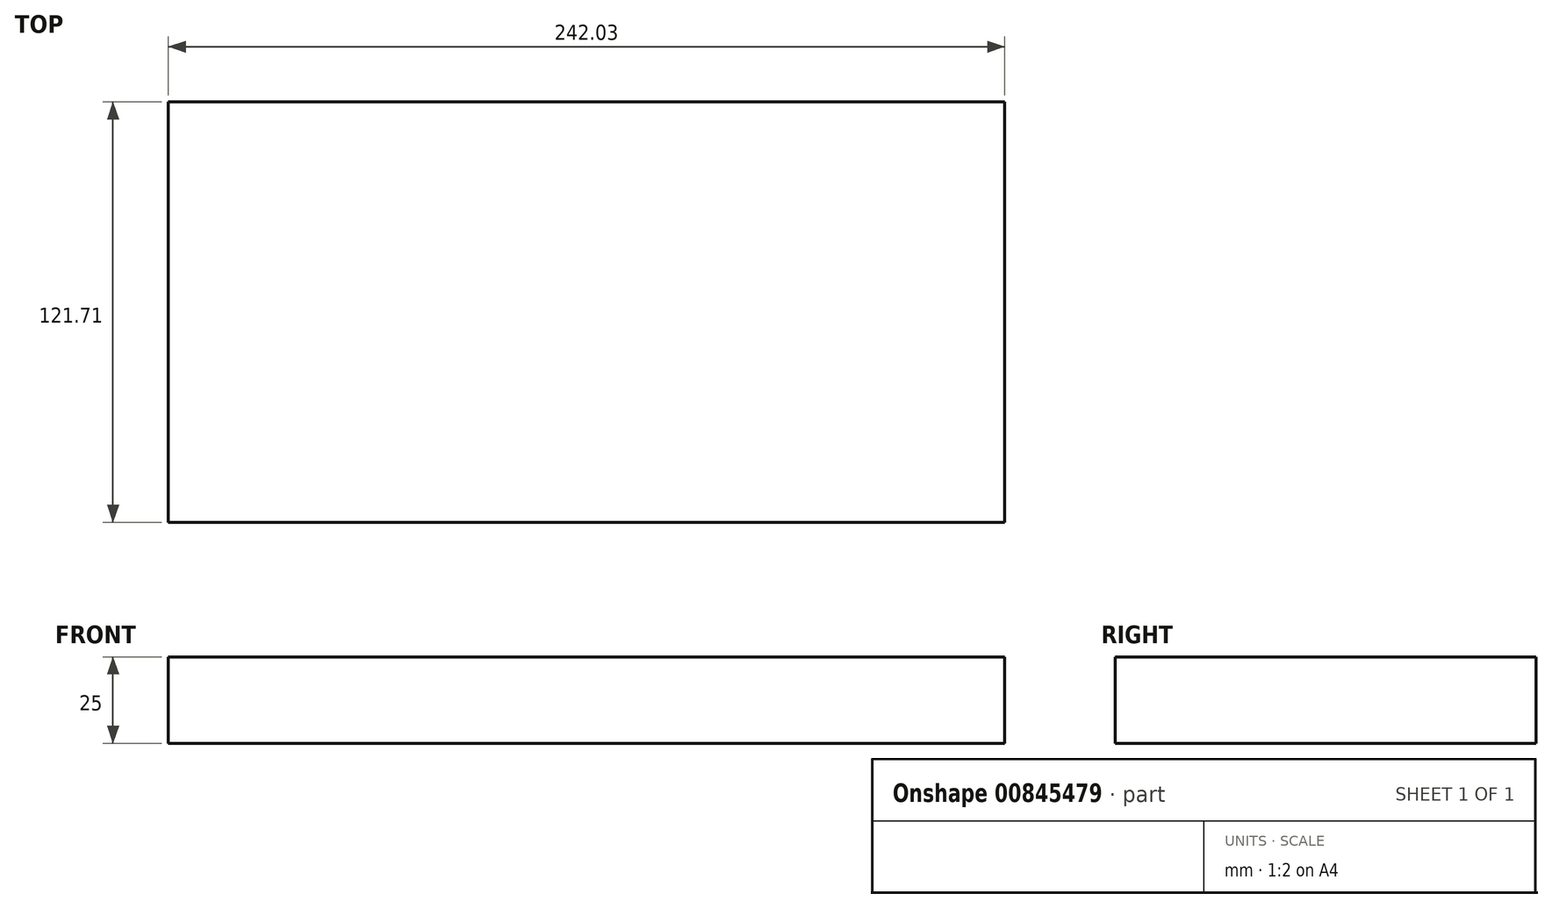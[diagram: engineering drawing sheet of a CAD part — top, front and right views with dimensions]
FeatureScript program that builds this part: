
annotation { "Feature Type Name" : "Feature", "Feature Type Description" : "" }
export const myFeature = defineFeature(function(context is Context, id is Id, definition is map)
    precondition{}
    {
        {
            var Q0;
            Q0=qCreatedBy(makeId("Top.planeOp"),FACE);
            var sketch = newSketch(context, id + "F0", { "sketchPlane" : qUnion([Q0])});
            skLineSegment(sketch, "E0.bottom", {"start": v(-113.02, 61.92) * mm, "end": v(129.01, 61.92) * mm});
            skLineSegment(sketch, "E0.top", {"start": v(-113.02, -59.79) * mm, "end": v(129.01, -59.79) * mm});
            skLineSegment(sketch, "E0.left", {"start": v(-113.02, 61.92) * mm, "end": v(-113.02, -59.79) * mm});
            skLineSegment(sketch, "E0.right", {"start": v(129.01, 61.92) * mm, "end": v(129.01, -59.79) * mm});
            skSolve(sketch);
        }
        {
            var Q0;
            Q0=makeQuery(id+"F0.imprint","IMPRINT",FACE,{"disambiguationData":[TD([[makeQuery(id+"F0.imprint","IMPRINT",EDGE,{"derivedFrom":sQuery(id+"F0.wireOp",EDGE,"E0.bottom")}),-1.0]])]});
            extrude(context, id + "F1", {"entities" : qUnion([Q0]), "depth" : 25 * mm, "offsetDistance" : 25 * mm});
        }
    });
